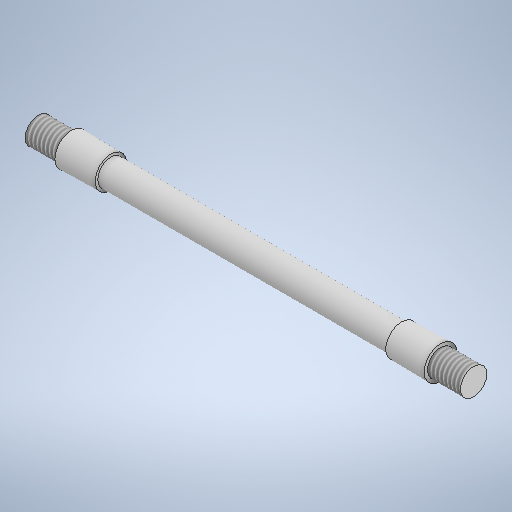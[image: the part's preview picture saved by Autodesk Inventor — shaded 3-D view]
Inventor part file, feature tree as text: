
AUTODESK INVENTOR PART (.ipt)
format: ipt  version: 2025.1 (Build 291241000, 241)  size: 284,160 bytes
history: native  units: mm
features: revolve x1, thread x1, sketch x1
ambient origin geometry x8: Origin, YZ Plane, XZ Plane, XY Plane, X Axis, Y Axis, Z Axis, Center Point
bodies: Volumenkörper1 (feature_tree)
feature tree (3):
  revolve  "Umdrehung1"
  thread  "Gewinde1"  [1 undecoded]
  sketch  "Skizze1"  dims[d2=10.0mm d3=10.0mm d4=12.0mm d5=8.0mm d6=0.174533mm d7=100.0mm d8=17.453293mm d9=360.0deg d10=132.0mm d11=0.0mm d12=12.0mm d13=10.0mm]
note: 1 required parameter value undecoded (feature->parameter linkage not recoverable at this tier; creation-order binding heuristic only, values carry confidence <= 0.55)
